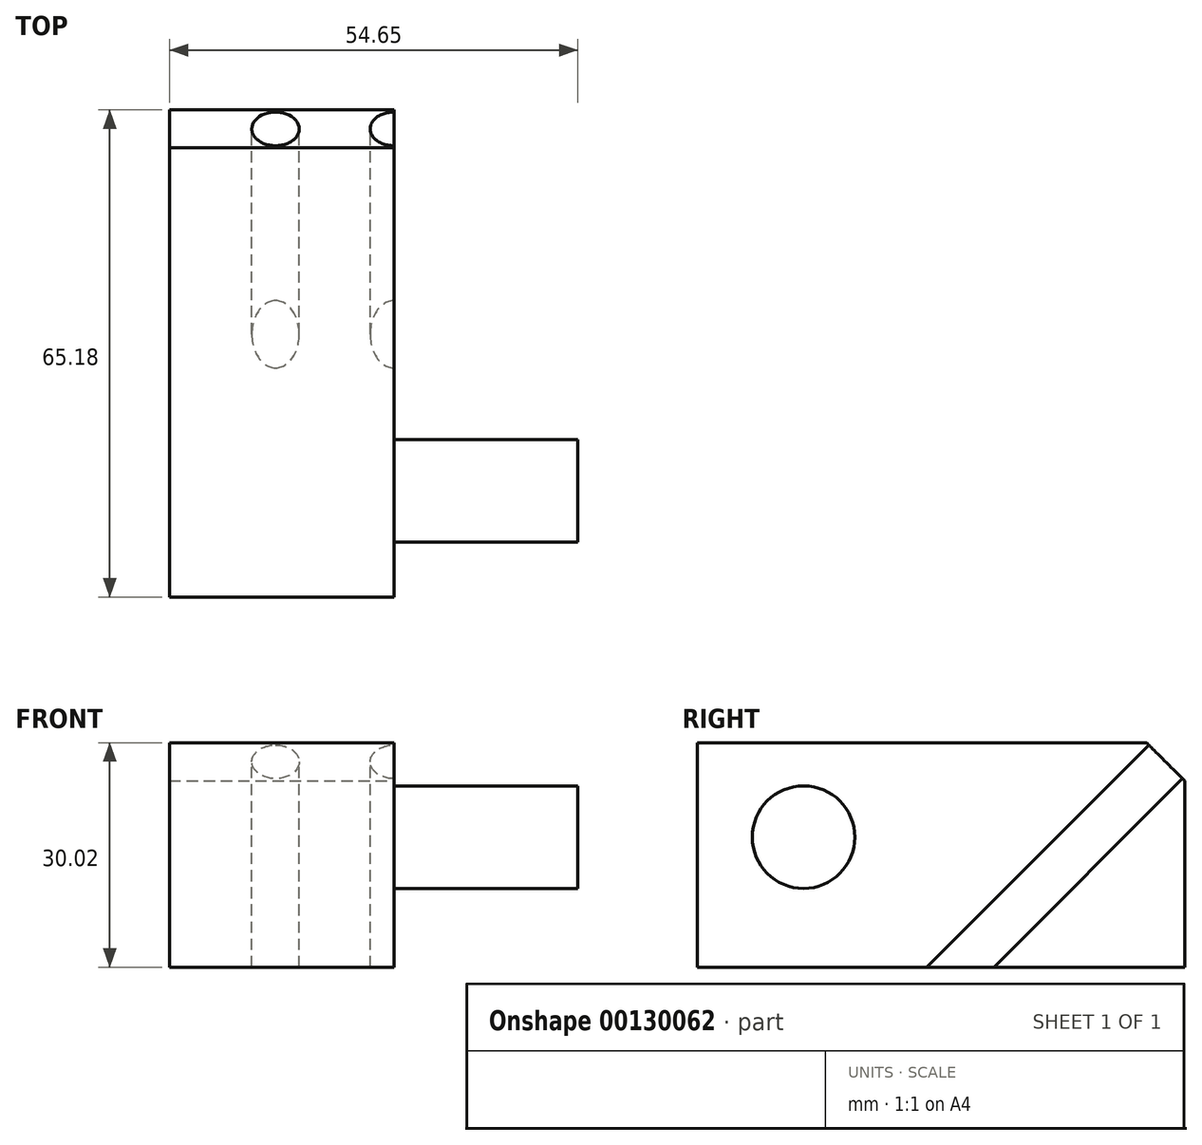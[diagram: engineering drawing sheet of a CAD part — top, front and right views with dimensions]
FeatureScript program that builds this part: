
annotation { "Feature Type Name" : "Feature", "Feature Type Description" : "" }
export const myFeature = defineFeature(function(context is Context, id is Id, definition is map)
    precondition{}
    {
        {
            var Q0;
            Q0=qCreatedBy(makeId("Front.planeOp"),FACE);
            var sketch = newSketch(context, id + "F0", { "sketchPlane" : qUnion([Q0])});
            skLineSegment(sketch, "E0.bottom", {"start": v(0, 0) * mm, "end": v(30.03, 0) * mm});
            skLineSegment(sketch, "E0.top", {"start": v(0, 30.02) * mm, "end": v(30.03, 30.02) * mm});
            skLineSegment(sketch, "E0.left", {"start": v(0, 0) * mm, "end": v(0, 30.02) * mm});
            skLineSegment(sketch, "E0.right", {"start": v(30.03, 0) * mm, "end": v(30.03, 30.02) * mm});
            skSolve(sketch);
        }
        {
            var Q0;
            Q0 = qSketchRegion(id + "F0", true);
            extrude(context, id + "F1", {"entities" : qUnion([Q0]), "depth" : 65.18 * mm});
        }
        {
            var Q0;
            Q0=makeQuery(id+"F1.opExtrude","SWEPT_FACE",FACE,{"disambiguationData":[OSD([sQuery(id+"F0.wireOp",EDGE,"E0.right")])]});
            var sketch = newSketch(context, id + "F2", { "sketchPlane" : qUnion([Q0])});
            skCircle(sketch, "E1", {"center": v(-50.98, 17.4) * mm, "radius": 6.86 * mm});
            skSolve(sketch);
        }
        {
            var Q0;
            Q0=makeQuery(id+"F2.imprint","IMPRINT",FACE,{"disambiguationData":[TD([[makeQuery(id+"F2.imprint","IMPRINT",EDGE,{"derivedFrom":sQuery(id+"F2.wireOp",EDGE,"E1")}),1.0]])]});
            extrude(context, id + "F3", {"entities" : qUnion([Q0]), "operationType" : NewBodyOperationType.ADD, "depth" : 24.62 * mm});
        }
        {
            var Q0;
            Q0=makeQuery(id+"F1.opExtrude","CAP_EDGE",EDGE,{"disambiguationData":[OSD([sQuery(id+"F0.wireOp",EDGE,"E0.top")])],"isStart":true});
            chamfer(context, id + "F4", {"entities" : qUnion([Q0]), "width" : 5.08 * mm, "tangentPropagation" : true});
        }
        {
            var Q0;
            Q0=makeQuery(id+"F4.opChamfer","BLEND_FACE",FACE,{"disambiguationData":[OSD([sQuery(id+"F0.wireOp",EDGE,"E0.top")])]});
            var sketch = newSketch(context, id + "F5", { "sketchPlane" : qUnion([Q0])});
            skCircle(sketch, "E2", {"center": v(-14.2, 21.22) * mm, "radius": 3 * mm});
            skPoint(sketch, "E2.centerSnap0", {"position": v(-30.03, 21.22) * mm});
            skSolve(sketch);
        }
        {
            var Q0;
            Q0=sQuery(id+"F5.wireOp",VERTEX,"E2.center");
            var Q1;
            Q1=sQuery(id+"F5.wireOp",VERTEX,"E2.centerSnap0");
            var Q2;
            Q2=makeQuery(id+"F1.opExtrude","SWEPT_BODY",BODY,{"disambiguationData":[OSD([sQuery(id+"F0.wireOp",EDGE,"E0.bottom"),sQuery(id+"F0.wireOp",EDGE,"E0.top"),sQuery(id+"F0.wireOp",EDGE,"E0.left"),sQuery(id+"F0.wireOp",EDGE,"E0.right")])]});
            hole(context, id + "F6", {"style" : HoleStyle.SIMPLE, "endStyle" : HoleEndStyle.THROUGH, "holeDiameter" : 6.35 * mm, "locations" : qUnion([Q0, Q1]), "scope" : qUnion([Q2]), "isTappedThrough" : true});
        }
    });
